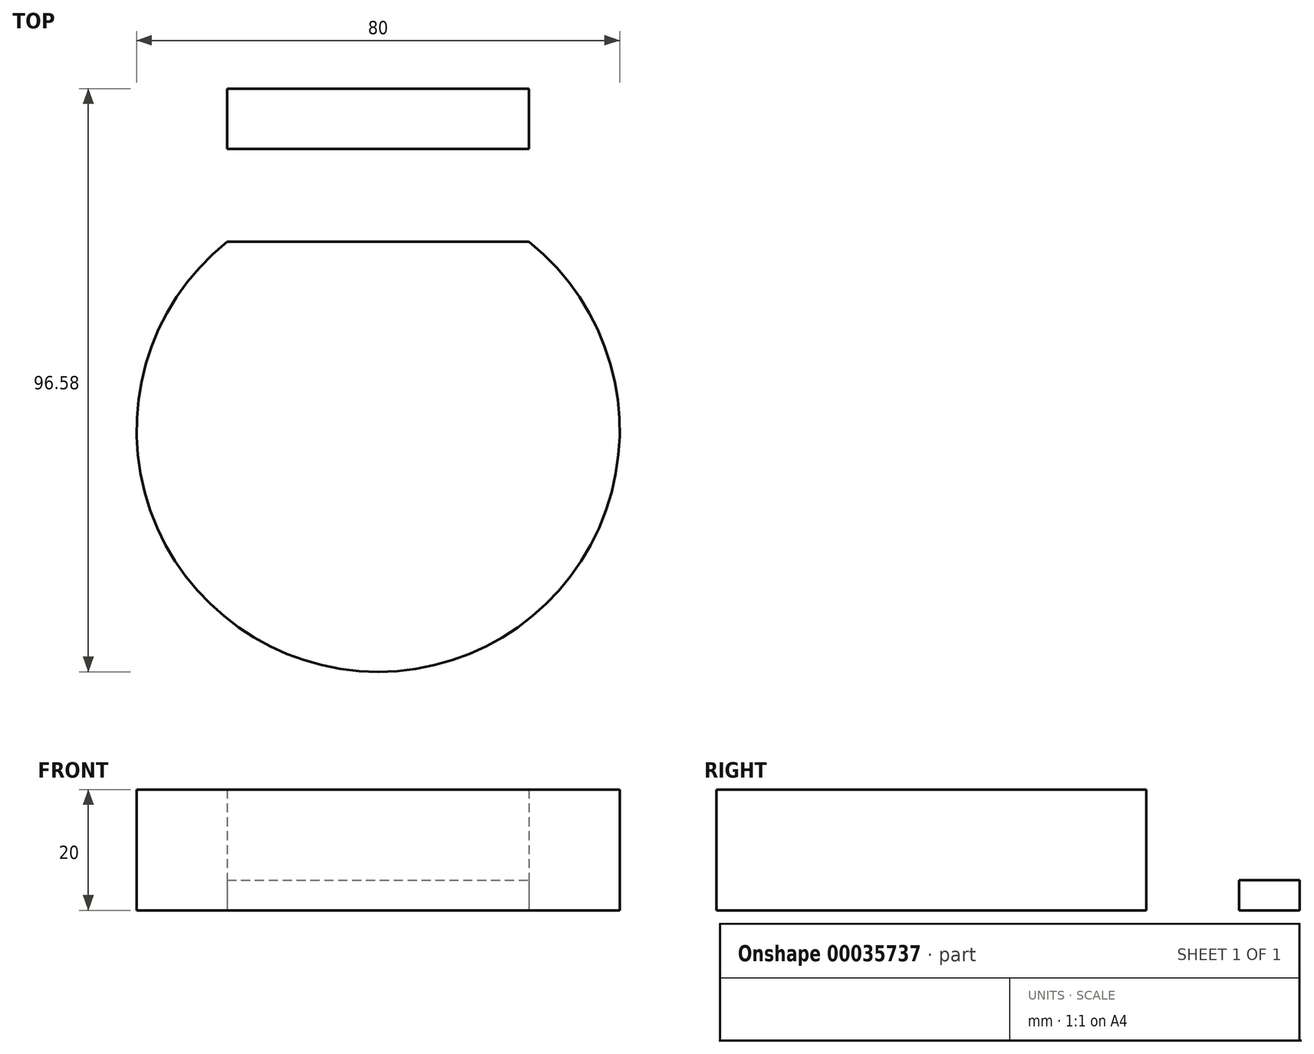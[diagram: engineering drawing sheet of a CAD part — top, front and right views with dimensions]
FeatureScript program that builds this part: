
annotation { "Feature Type Name" : "Feature", "Feature Type Description" : "" }
export const myFeature = defineFeature(function(context is Context, id is Id, definition is map)
    precondition{}
    {
        {
            var Q0;
            Q0=qCreatedBy(makeId("Top.planeOp"),FACE);
            var sketch = newSketch(context, id + "F0", { "sketchPlane" : qUnion([Q0])});
            skArc(sketch, "E0", {"start": v(-25, 31.22) * mm, "mid": v(0, -40) * mm, "end": v(25, 31.22) * mm});
            skLineSegment(sketch, "E1", {"start": v(-25, 31.22) * mm, "end": v(25, 31.22) * mm});
            skLineSegment(sketch, "E2.bottom", {"start": v(-25, 56.58) * mm, "end": v(25, 56.58) * mm});
            skLineSegment(sketch, "E2.top", {"start": v(-25, 46.58) * mm, "end": v(25, 46.58) * mm});
            skLineSegment(sketch, "E2.left", {"start": v(-25, 56.58) * mm, "end": v(-25, 46.58) * mm});
            skLineSegment(sketch, "E2.right", {"start": v(25, 56.58) * mm, "end": v(25, 46.58) * mm});
            skSolve(sketch);
        }
        {
            var Q0;
            Q0=makeQuery(id+"F0.imprint","IMPRINT",FACE,{"disambiguationData":[TD([[makeQuery(id+"F0.imprint","IMPRINT",EDGE,{"derivedFrom":sQuery(id+"F0.wireOp",EDGE,"E0")}),1.0]])]});
            extrude(context, id + "F1", {"entities" : qUnion([Q0]), "depth" : 20 * mm});
        }
        {
            var Q0;
            Q0=makeQuery(id+"F0.imprint","IMPRINT",FACE,{"disambiguationData":[TD([[makeQuery(id+"F0.imprint","IMPRINT",EDGE,{"derivedFrom":sQuery(id+"F0.wireOp",EDGE,"E2.bottom")}),-1.0]])]});
            extrude(context, id + "F2", {"entities" : qUnion([Q0]), "depth" : 5 * mm});
        }
    });
